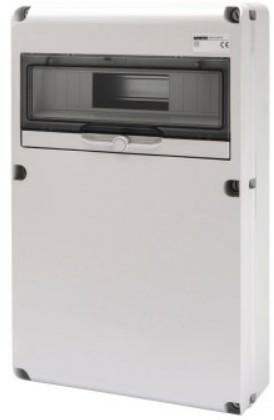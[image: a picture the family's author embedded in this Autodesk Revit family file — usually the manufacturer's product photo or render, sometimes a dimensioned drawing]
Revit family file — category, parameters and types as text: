
# Revit family: Building-QuadriIEC309-GEWISS-68QDIN-QUADRI-PRESE-14MOD_CIECO_DOPPIO
name_source: partatom
category: Apparecchi elettrici
units: mm (PartAtom-declared; Revit-internal decimal feet)

## family parameters
Condiviso = No
Host = Superficie
Mantenere orientamento annotazione = Sì
Punto di calcolo locali = Sì
Quota connettore circolare = Usa diametro
Taglio con vuoti quando caricato = No
Tipo di parte = Normale

## types (1)
- GW68007N - Q-DIN 14M COP.CIECO 510x320x135 IP65
    Catalogo = BUILDING
    Catalogo Serie = 68 QDIN
    Classe isolamento = II
    Codice EAN = 8011564744783
    Codice Electrocod = 2242
    Colore = Grigio RAL 7035
    Conformità normativa = EN 60208 - EN 60670-1 - IEC 60670-24
    Descrizione = Q-DIN 14M COP.CIECO 510x320x135 IP65
    Glow Wire Test = 650°C
    Grado di protezione = IP65
    IDF = 98e9c67e-2f70-4624-9f1a-35073c126d72
    IDT = 5858c0d8-961a-4254-a97b-2dfffa1f665c
    Immagine tipo = GW68007N.jpg
    L_Moduli = 266 mm  [stored 0.872703 ft]
    Modello = GW68007N
    N. coperchi ciechi in dotazione = -
    N. mod. EN 50022 = 14
    N. prese alloggiabili = Coperchio cieco
    N_Moduli = 14 mm  [stored 0.0459318 ft]
    POMELLO = bianco
    PRESA = rosso
    Potenza dissipabile A (W) = 24
    Potenza dissipabile B (W) = 64
    Produttore = GEWISS S.p.A.
    Prospetto di default = 1219 mm
    Resistenza agli urti = IK09
    SEO = Quadretto
    STRUTTURA = RAL - 7035
    STRUTTURA ALTA = Poche
    Scheda Tecnica = https://www.gewiss.com
    Spostamento_S = 1000 mm  [stored 3.28084 ft]
    Temperatura di utilizzo = -25 +40 °C
    Termopressione con biglia = 70 °C
    Tipo versione = Vuoto
    Tipologia di installazione = Da parete
    URL = https://www.gewiss.com
    VETRO = Vetro
    Versione file RFA = 21.5

note: [stored X ft] marks values corroborated as IEEE doubles in the binary element streams (Revit-internal decimal feet)

## geometry (parser evidence)
native form markers: Sweep x3
no freeform markers — native parametric forms only
